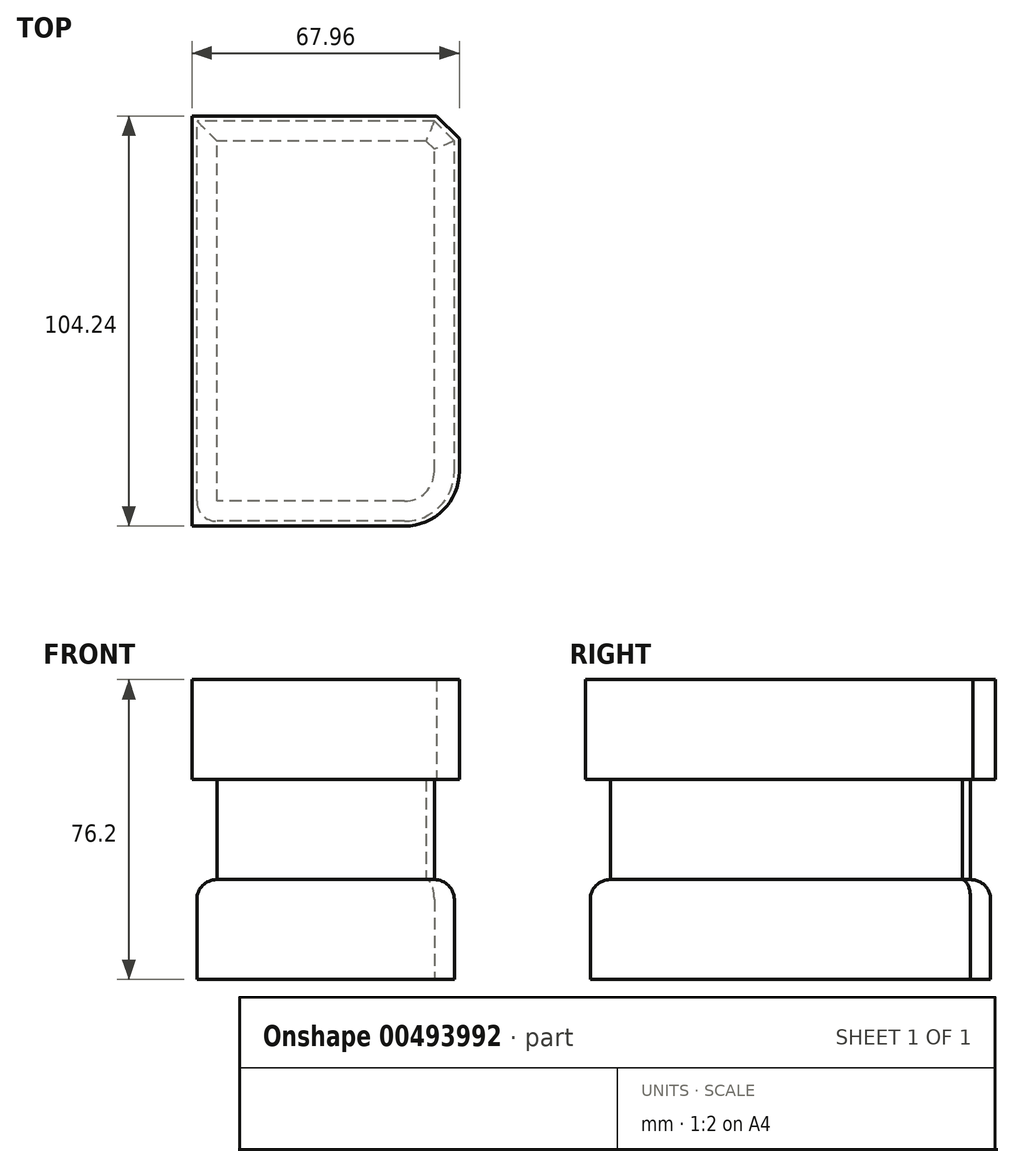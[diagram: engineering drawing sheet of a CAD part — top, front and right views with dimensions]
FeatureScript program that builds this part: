
annotation { "Feature Type Name" : "Feature", "Feature Type Description" : "" }
export const myFeature = defineFeature(function(context is Context, id is Id, definition is map)
    precondition{}
    {
        {
            var Q0;
            Q0=qCreatedBy(makeId("Top.planeOp"),FACE);
            var sketch = newSketch(context, id + "F0", { "sketchPlane" : qUnion([Q0])});
            skLineSegment(sketch, "E0.bottom", {"start": v(32.7, -50.85) * mm, "end": v(-32.7, -50.85) * mm});
            skLineSegment(sketch, "E0.top", {"start": v(32.7, 50.85) * mm, "end": v(-32.7, 50.85) * mm});
            skLineSegment(sketch, "E0.left", {"start": v(32.7, -50.85) * mm, "end": v(32.7, 50.85) * mm});
            skLineSegment(sketch, "E0.right", {"start": v(-32.7, -50.85) * mm, "end": v(-32.7, 50.85) * mm});
            skPoint(sketch, "E0.middle", {"position": v(0, 0) * mm});
            skSolve(sketch);
        }
        {
            var Q0;
            Q0 = qSketchRegion(id + "F0", true);
            extrude(context, id + "F1", {"entities" : qUnion([Q0]), "depth" : 25.4 * mm});
        }
        {
            var Q0;
            Q0=makeQuery(id+"F1.opExtrude","SWEPT_EDGE",EDGE,{"disambiguationData":[OSD([sQuery(id+"F0.wireOp",EDGE,"E0.top"),sQuery(id+"F0.wireOp",EDGE,"E0.left")])]});
            chamfer(context, id + "F2", {"entities" : qUnion([Q0]), "width" : 5.08 * mm, "tangentPropagation" : true});
        }
        {
            var Q0;
            Q0=makeQuery(id+"F1.opExtrude","SWEPT_EDGE",EDGE,{"disambiguationData":[OSD([sQuery(id+"F0.wireOp",EDGE,"E0.bottom"),sQuery(id+"F0.wireOp",EDGE,"E0.right")])]});
            fillet(context, id + "F3", {"entities" : qUnion([Q0]), "radius" : 5.08 * mm, "tangentPropagation" : true, "allowEdgeOverflow" : false});
        }
        {
            var Q0;
            Q0=makeQuery(id+"F1.opExtrude","SWEPT_EDGE",EDGE,{"disambiguationData":[OSD([sQuery(id+"F0.wireOp",EDGE,"E0.bottom"),sQuery(id+"F0.wireOp",EDGE,"E0.left")])]});
            fillet(context, id + "F4", {"entities" : qUnion([Q0]), "radius" : 12.7 * mm, "tangentPropagation" : true, "allowEdgeOverflow" : false});
        }
        {
            var Q0;
            Q0=makeQuery(id+"F1.opExtrude","CAP_EDGE",EDGE,{"disambiguationData":[OSD([sQuery(id+"F0.wireOp",EDGE,"E0.left")])],"isStart":false});
            var Q1;
            Q1=makeQuery(id+"F1.opExtrude","CAP_EDGE",EDGE,{"disambiguationData":[OSD([sQuery(id+"F0.wireOp",EDGE,"E0.bottom")])],"isStart":false});
            var Q2;
            Q2=makeQuery(id+"F1.opExtrude","CAP_FACE",FACE,{"disambiguationData":[OSD([sQuery(id+"F0.wireOp",EDGE,"E0.bottom"),sQuery(id+"F0.wireOp",EDGE,"E0.top"),sQuery(id+"F0.wireOp",EDGE,"E0.left"),sQuery(id+"F0.wireOp",EDGE,"E0.right")])],"isStart":false});
            fillet(context, id + "F5", {"entities" : qUnion([Q0, Q1, Q2]), "radius" : 5.08 * mm, "tangentPropagation" : true, "allowEdgeOverflow" : false});
        }
        {
            var Q0;
            Q0=makeQuery(id+"F1.opExtrude","CAP_FACE",FACE,{"disambiguationData":[OSD([sQuery(id+"F0.wireOp",EDGE,"E0.bottom"),sQuery(id+"F0.wireOp",EDGE,"E0.top"),sQuery(id+"F0.wireOp",EDGE,"E0.left"),sQuery(id+"F0.wireOp",EDGE,"E0.right")])],"isStart":false});
            extrude(context, id + "F6", {"entities" : qUnion([Q0]), "operationType" : NewBodyOperationType.ADD, "depth" : 25.4 * mm});
        }
        {
            var Q0;
            Q0=makeQuery(id+"F6.opExtrude","CAP_FACE",FACE,{"disambiguationData":[OSD([sQuery(id+"F0.wireOp",EDGE,"E0.bottom"),sQuery(id+"F0.wireOp",EDGE,"E0.top"),sQuery(id+"F0.wireOp",EDGE,"E0.left"),sQuery(id+"F0.wireOp",EDGE,"E0.right")])],"isStart":false});
            var sketch = newSketch(context, id + "F7", { "sketchPlane" : qUnion([Q0])});
            skLineSegment(sketch, "E1.0", {"start": v(-33.98, 52.12) * mm, "end": v(-33.98, -52.12) * mm});
            skArc(sketch, "E1.1", {"start": v(20, -52.12) * mm, "mid": v(29.89, -48.03) * mm, "end": v(33.98, -38.15) * mm});
            skLineSegment(sketch, "E1.2", {"start": v(33.98, -38.15) * mm, "end": v(33.98, 46.3) * mm});
            skLineSegment(sketch, "E1.3", {"start": v(-33.98, -52.12) * mm, "end": v(20, -52.12) * mm});
            skLineSegment(sketch, "E1.4", {"start": v(33.98, 46.3) * mm, "end": v(28.16, 52.12) * mm});
            skLineSegment(sketch, "E1.5", {"start": v(28.16, 52.12) * mm, "end": v(-33.98, 52.12) * mm});
            skSolve(sketch);
        }
        {
            var Q0;
            Q0 = qSketchRegion(id + "F7", true);
            extrude(context, id + "F8", {"entities" : qUnion([Q0]), "operationType" : NewBodyOperationType.ADD, "depth" : 25.4 * mm});
        }
    });
